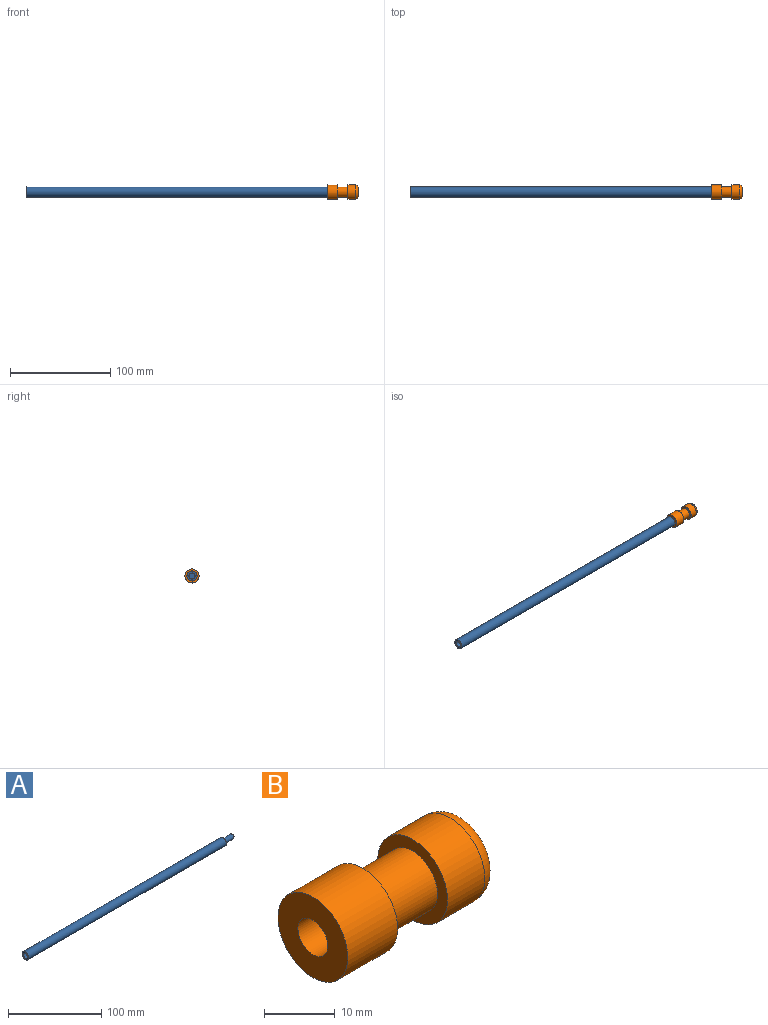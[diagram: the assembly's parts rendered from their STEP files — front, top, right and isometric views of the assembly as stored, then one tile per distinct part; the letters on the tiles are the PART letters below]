
ASSEMBLY  parts=2 mates=1
PART A: 8 faces, bbox 315x10x10 mm
  f0: cylinder r=5mm len=300mm, axis (-1,0,0), area 9424.8mm2, adj f1,f2
  f1: plane 10x10mm, normal (1,0,0), area 50.3mm2, adj f0,f3
  f2: plane 10x10mm, normal (-1,0,0), area 50.3mm2, adj f0,f5
  f3: cylinder r=3mm len=13.5mm, axis (-1,0,0), area 254.5mm2, adj f1,f7
  f4: plane 3x3mm, normal (1,0,0), area 7.1mm2, adj f7
  f5: cylinder r=3mm len=15mm, axis (-1,0,0), area 282.7mm2, adj f2,f6
  f6: plane 6x6mm, normal (-1,0,0), area 28.3mm2, adj f5
  f7: cone r=1.5mm half-angle=45deg, axis (-1,0,0), area 30mm2, adj f3,f4
PART B: 10 faces, bbox 30x15.2x15.2 mm
  f0: cylinder r=7mm len=14mm, axis (-1,0,0), area 439.8mm2, adj f1,f2
  f1: plane 14x14mm, normal (1,0,0), area 75.4mm2, adj f0,f4
  f2: plane 14x14mm, normal (-1,0,0), area 125.7mm2, adj f0,f3
  f3: cylinder r=3mm len=20mm, axis (-1,0,0), area 377mm2, adj f2,f9
  f4: cylinder r=5mm len=10mm, axis (-1,0,0), area 314.2mm2, adj f1,f7
  f5: cylinder r=7mm len=14mm, axis (-1,0,0), area 329.9mm2, adj f7,f8
  f6: plane 9x9mm, normal (1,0,0), area 63.6mm2, adj f8
  f7: plane 14x14mm, normal (-1,0,0), area 75.4mm2, adj f4,f5
  f8: torus R=4.5mm, axis (1,0,0), area 150.3mm2, adj f5,f6
  f9: plane 6x6mm, normal (-1,0,0), area 28.3mm2, adj f3
PLACE A t=(-70.12,61.57,-30.68)mm
PLACE B t=(230.42,110.26,-30.68)mm
MATE slider B.f0 <-> A.f3  axis (-1,0,0) through (230.42,61.57,-30.68)mm
